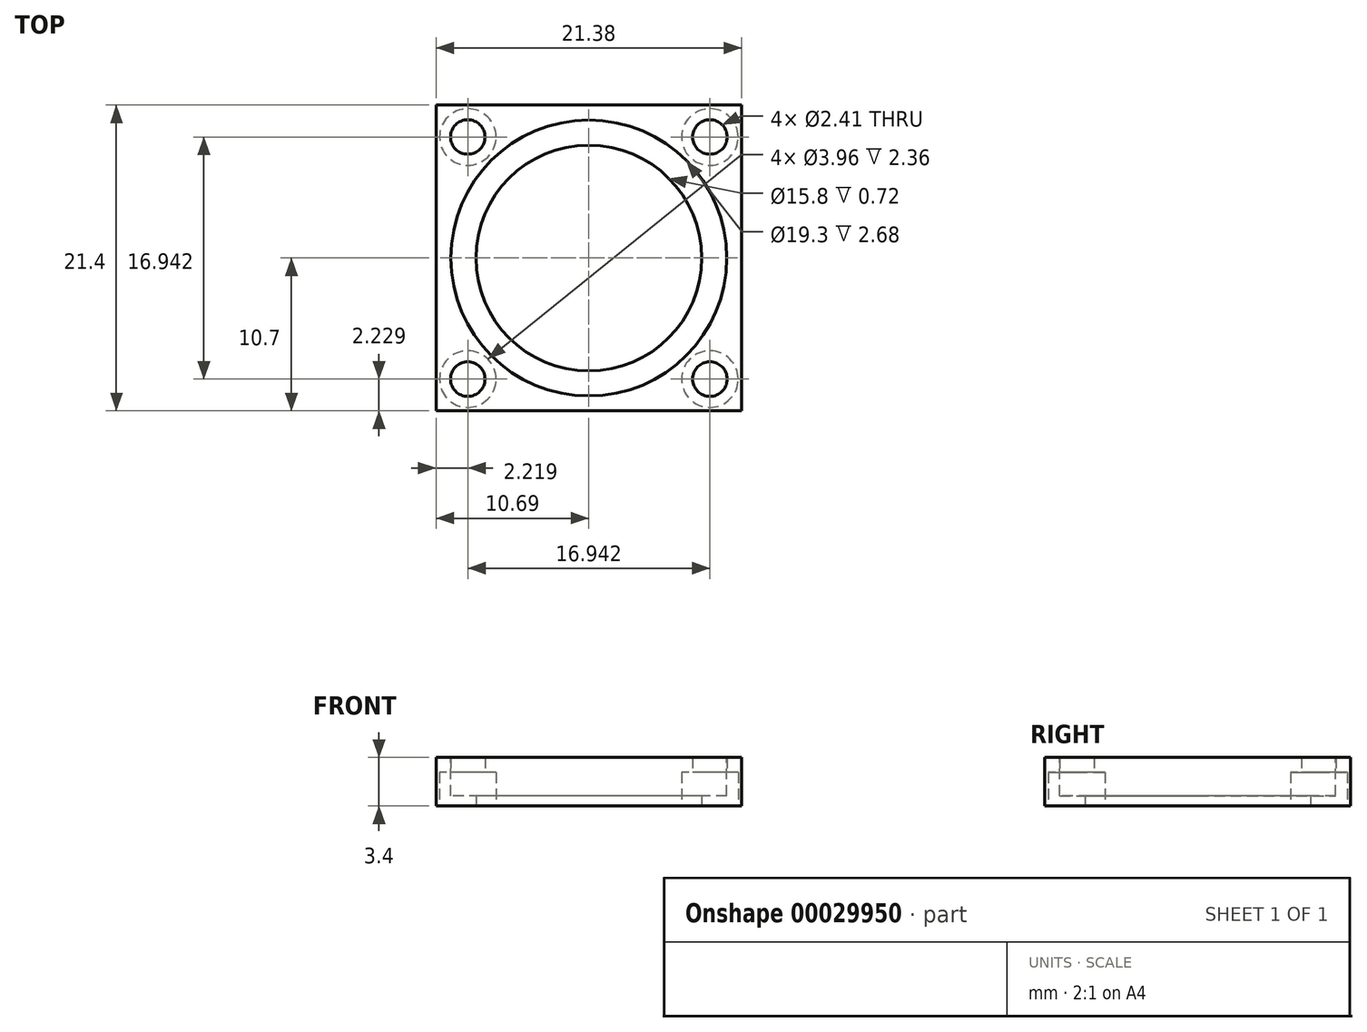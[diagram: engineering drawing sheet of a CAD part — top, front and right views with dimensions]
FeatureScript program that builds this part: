
annotation { "Feature Type Name" : "Feature", "Feature Type Description" : "" }
export const myFeature = defineFeature(function(context is Context, id is Id, definition is map)
    precondition{}
    {
        {
            var Q0;
            Q0=qCreatedBy(makeId("Top.planeOp"),FACE);
            var sketch = newSketch(context, id + "F0", { "sketchPlane" : qUnion([Q0])});
            skCircle(sketch, "E0.1.0.1", {"center": v(8.47, 8.47) * mm, "radius": 1.98 * mm});
            skCircle(sketch, "E0.1.1.0", {"center": v(8.47, -8.47) * mm, "radius": 1.2 * mm});
            skCircle(sketch, "E0.1.1.1", {"center": v(8.47, -8.47) * mm, "radius": 1.98 * mm});
            skCircle(sketch, "E1", {"center": v(-8.47, 8.47) * mm, "radius": 1.2 * mm});
            skLineSegment(sketch, "E2.rect.bottom", {"start": v(-10.7, 10.7) * mm, "end": v(10.7, 10.7) * mm});
            skLineSegment(sketch, "E2.rect.top", {"start": v(-10.7, -10.7) * mm, "end": v(10.69, -10.7) * mm});
            skLineSegment(sketch, "E2.rect.left", {"start": v(-10.7, 10.7) * mm, "end": v(-10.7, -10.7) * mm});
            skLineSegment(sketch, "E2.rect.right", {"start": v(10.7, 10.7) * mm, "end": v(10.69, -10.7) * mm});
            skCircle(sketch, "E3", {"center": v(-8.47, 8.47) * mm, "radius": 1.98 * mm});
            skLineSegment(sketch, "E4.rect.top", {"start": v(-8.47, -8.47) * mm, "end": v(8.47, -8.47) * mm, "construction": true});
            skLineSegment(sketch, "E4.rect.right", {"start": v(8.47, 8.47) * mm, "end": v(8.47, -8.47) * mm, "construction": true});
            skCircle(sketch, "E0.0.1.0", {"center": v(-8.47, -8.47) * mm, "radius": 1.2 * mm});
            skCircle(sketch, "E0.0.1.1", {"center": v(-8.47, -8.47) * mm, "radius": 1.98 * mm});
            skCircle(sketch, "E0.1.0.0", {"center": v(8.47, 8.47) * mm, "radius": 1.2 * mm});
            skCircle(sketch, "E5", {"center": v(0, 0) * mm, "radius": 7.9 * mm});
            skSolve(sketch);
        }
        {
            var Q0;
            Q0=makeQuery(id+"F0.imprint","IMPRINT",FACE,{"disambiguationData":[TD([[makeQuery(id+"F0.imprint","IMPRINT",EDGE,{"derivedFrom":sQuery(id+"F0.wireOp",EDGE,"E0.1.0.1")}),-1.0]])]});
            var Q1;
            Q1=makeQuery(id+"F0.imprint","IMPRINT",FACE,{"disambiguationData":[TD([[makeQuery(id+"F0.imprint","IMPRINT",EDGE,{"derivedFrom":sQuery(id+"F0.wireOp",EDGE,"E0.0.1.0")}),-1.0]])]});
            var Q2;
            Q2=makeQuery(id+"F0.imprint","IMPRINT",FACE,{"disambiguationData":[TD([[makeQuery(id+"F0.imprint","IMPRINT",EDGE,{"derivedFrom":sQuery(id+"F0.wireOp",EDGE,"E1")}),-1.0]])]});
            var Q3;
            Q3=makeQuery(id+"F0.imprint","IMPRINT",FACE,{"disambiguationData":[TD([[makeQuery(id+"F0.imprint","IMPRINT",EDGE,{"derivedFrom":sQuery(id+"F0.wireOp",EDGE,"E0.1.1.0")}),-1.0]])]});
            var Q4;
            Q4=makeQuery(id+"F0.imprint","IMPRINT",FACE,{"disambiguationData":[TD([[makeQuery(id+"F0.imprint","IMPRINT",EDGE,{"derivedFrom":sQuery(id+"F0.wireOp",EDGE,"E0.1.0.1")}),1.0]])]});
            extrude(context, id + "F1", {"entities" : qUnion([Q0, Q1, Q2, Q3, Q4]), "depth" : 3.4 * mm});
        }
        {
            var Q0;
            Q0=makeQuery(id+"F0.imprint","IMPRINT",FACE,{"disambiguationData":[TD([[makeQuery(id+"F0.imprint","IMPRINT",EDGE,{"derivedFrom":sQuery(id+"F0.wireOp",EDGE,"E0.0.1.0")}),-1.0]])]});
            var Q1;
            Q1=makeQuery(id+"F0.imprint","IMPRINT",FACE,{"disambiguationData":[TD([[makeQuery(id+"F0.imprint","IMPRINT",EDGE,{"derivedFrom":sQuery(id+"F0.wireOp",EDGE,"E0.1.1.0")}),-1.0]])]});
            var Q2;
            Q2=makeQuery(id+"F0.imprint","IMPRINT",FACE,{"disambiguationData":[TD([[makeQuery(id+"F0.imprint","IMPRINT",EDGE,{"derivedFrom":sQuery(id+"F0.wireOp",EDGE,"E0.1.0.1")}),1.0]])]});
            var Q3;
            Q3=makeQuery(id+"F0.imprint","IMPRINT",FACE,{"disambiguationData":[TD([[makeQuery(id+"F0.imprint","IMPRINT",EDGE,{"derivedFrom":sQuery(id+"F0.wireOp",EDGE,"E1")}),-1.0]])]});
            extrude(context, id + "F2", {"entities" : qUnion([Q0, Q1, Q2, Q3]), "operationType" : NewBodyOperationType.REMOVE, "depth" : 2.36 * mm});
        }
        {
            var Q0;
            Q0=makeQuery(id+"F1.opExtrude","CAP_FACE",FACE,{"disambiguationData":[OSD([sQuery(id+"F0.wireOp",EDGE,"E0.1.1.0"),sQuery(id+"F0.wireOp",EDGE,"E1"),sQuery(id+"F0.wireOp",EDGE,"E2.rect.bottom"),sQuery(id+"F0.wireOp",EDGE,"E2.rect.top"),sQuery(id+"F0.wireOp",EDGE,"E2.rect.left"),sQuery(id+"F0.wireOp",EDGE,"E2.rect.right"),sQuery(id+"F0.wireOp",EDGE,"E0.0.1.0"),sQuery(id+"F0.wireOp",EDGE,"E0.1.0.0"),sQuery(id+"F0.wireOp",EDGE,"E5")])],"isStart":false});
            var sketch = newSketch(context, id + "F3", { "sketchPlane" : qUnion([Q0])});
            skCircle(sketch, "E6", {"center": v(0, 0) * mm, "radius": 9.65 * mm});
            skSolve(sketch);
        }
        {
            var Q0;
            Q0=makeQuery(id+"F3.imprint","IMPRINT",FACE,{"disambiguationData":[TD([[makeQuery(id+"F3.imprint","IMPRINT",EDGE,{"derivedFrom":sQuery(id+"F3.wireOp",EDGE,"E6")}),1.0]])]});
            extrude(context, id + "F4", {"entities" : qUnion([Q0]), "operationType" : NewBodyOperationType.REMOVE, "oppositeDirection" : true, "depth" : 2.68 * mm});
        }
    });
